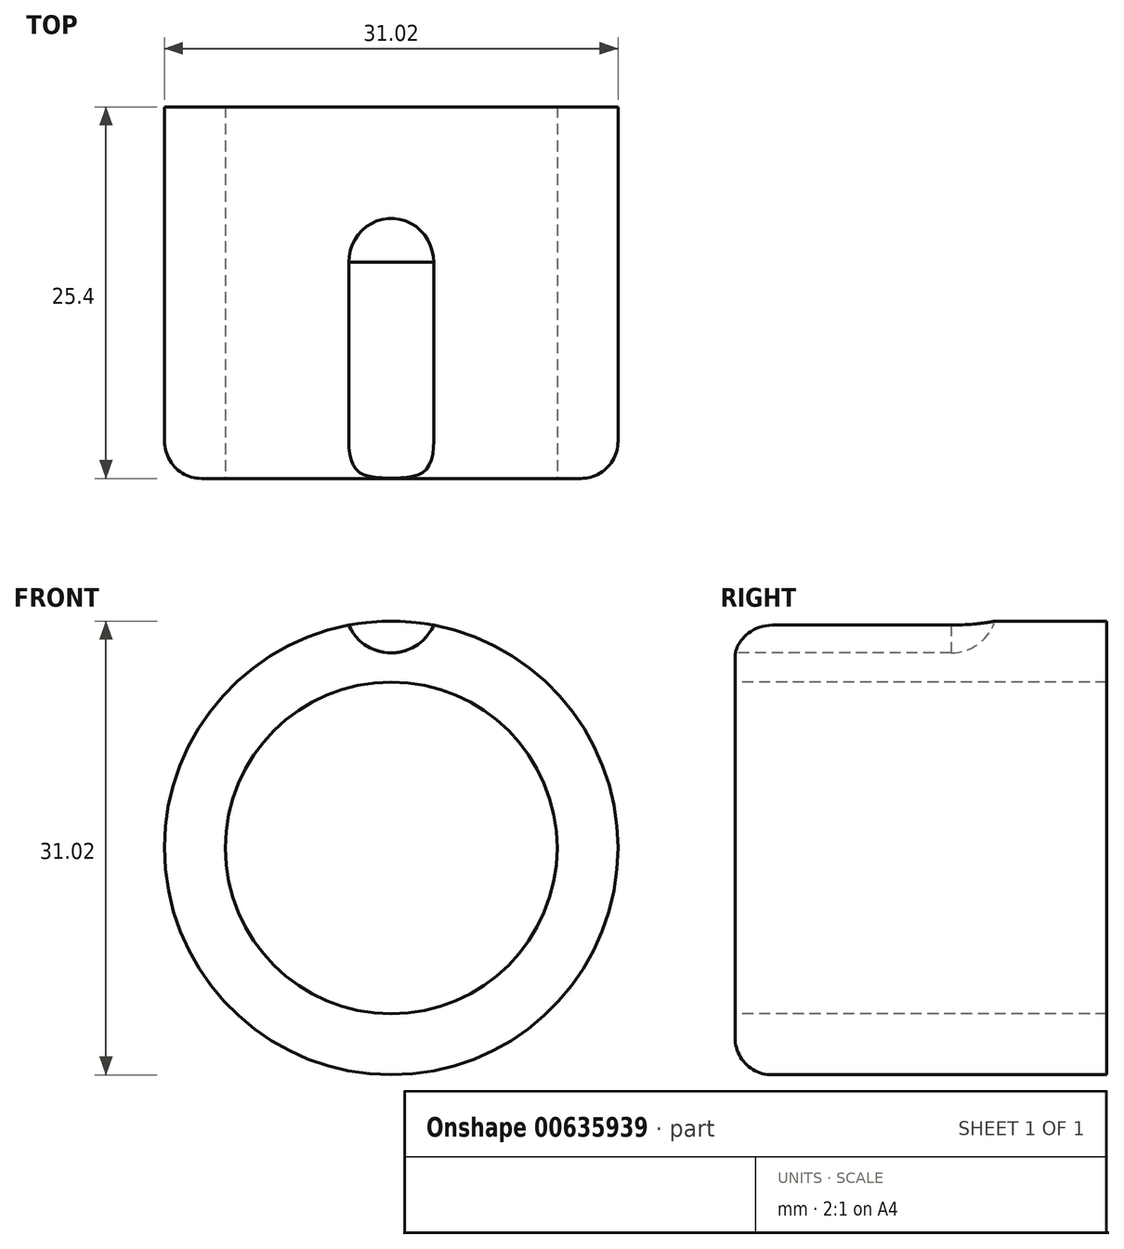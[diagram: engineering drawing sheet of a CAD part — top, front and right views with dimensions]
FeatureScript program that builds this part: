
annotation { "Feature Type Name" : "Feature", "Feature Type Description" : "" }
export const myFeature = defineFeature(function(context is Context, id is Id, definition is map)
    precondition{}
    {
        {
            var Q0;
            Q0=qCreatedBy(makeId("Front.planeOp"),FACE);
            var sketch = newSketch(context, id + "F0", { "sketchPlane" : qUnion([Q0])});
            skCircle(sketch, "E0", {"center": v(0, 0) * mm, "radius": 15.5 * mm});
            skCircle(sketch, "E1", {"center": v(0, 0) * mm, "radius": 11.34 * mm});
            skLineSegment(sketch, "E2", {"start": v(0, 24) * mm, "end": v(0, -25.13) * mm, "construction": true});
            skSolve(sketch);
        }
        {
            var Q0;
            Q0 = qSketchRegion(id + "F0", true);
            extrude(context, id + "F1", {"entities" : qUnion([Q0]), "oppositeDirection" : true, "depth" : 25.4 * mm, "offsetDistance" : 25.4 * mm});
        }
        {
            var Q0;
            Q0=makeQuery(id+"F1.opExtrude","CAP_EDGE",EDGE,{"disambiguationData":[OSD([sQuery(id+"F0.wireOp",EDGE,"E0")])],"isStart":true});
            fillet(context, id + "F2", {"entities" : qUnion([Q0]), "radius" : 2.54 * mm, "tangentPropagation" : true, "allowEdgeOverflow" : false});
        }
        {
            var Q0;
            Q0=makeQuery(id+"F1.opExtrude","CAP_FACE",FACE,{"disambiguationData":[OSD([sQuery(id+"F0.wireOp",EDGE,"E0"),sQuery(id+"F0.wireOp",EDGE,"E1")])],"isStart":true});
            var sketch = newSketch(context, id + "F3", { "sketchPlane" : qUnion([Q0])});
            skCircle(sketch, "E3", {"center": v(0, 16.51) * mm, "radius": 3.18 * mm});
            skSolve(sketch);
        }
        {
            var Q0;
            Q0 = qSketchRegion(id + "F3", true);
            extrude(context, id + "F4", {"entities" : qUnion([Q0]), "operationType" : NewBodyOperationType.REMOVE, "oppositeDirection" : true, "depth" : 17.78 * mm, "offsetDistance" : 25.4 * mm});
        }
        {
            var Q0;
            Q0=makeQuery(id+"F4.boolean.opBoolean","COPY",EDGE,{"derivedFrom":makeQuery(id+"F4.opExtrude","CAP_EDGE",EDGE,{"disambiguationData":[OSD([sQuery(id+"F3.wireOp",EDGE,"E3")])],"isStart":false})});
            fillet(context, id + "F5", {"entities" : qUnion([Q0]), "radius" : 3.17 * mm, "tangentPropagation" : true, "allowEdgeOverflow" : false});
        }
    });
